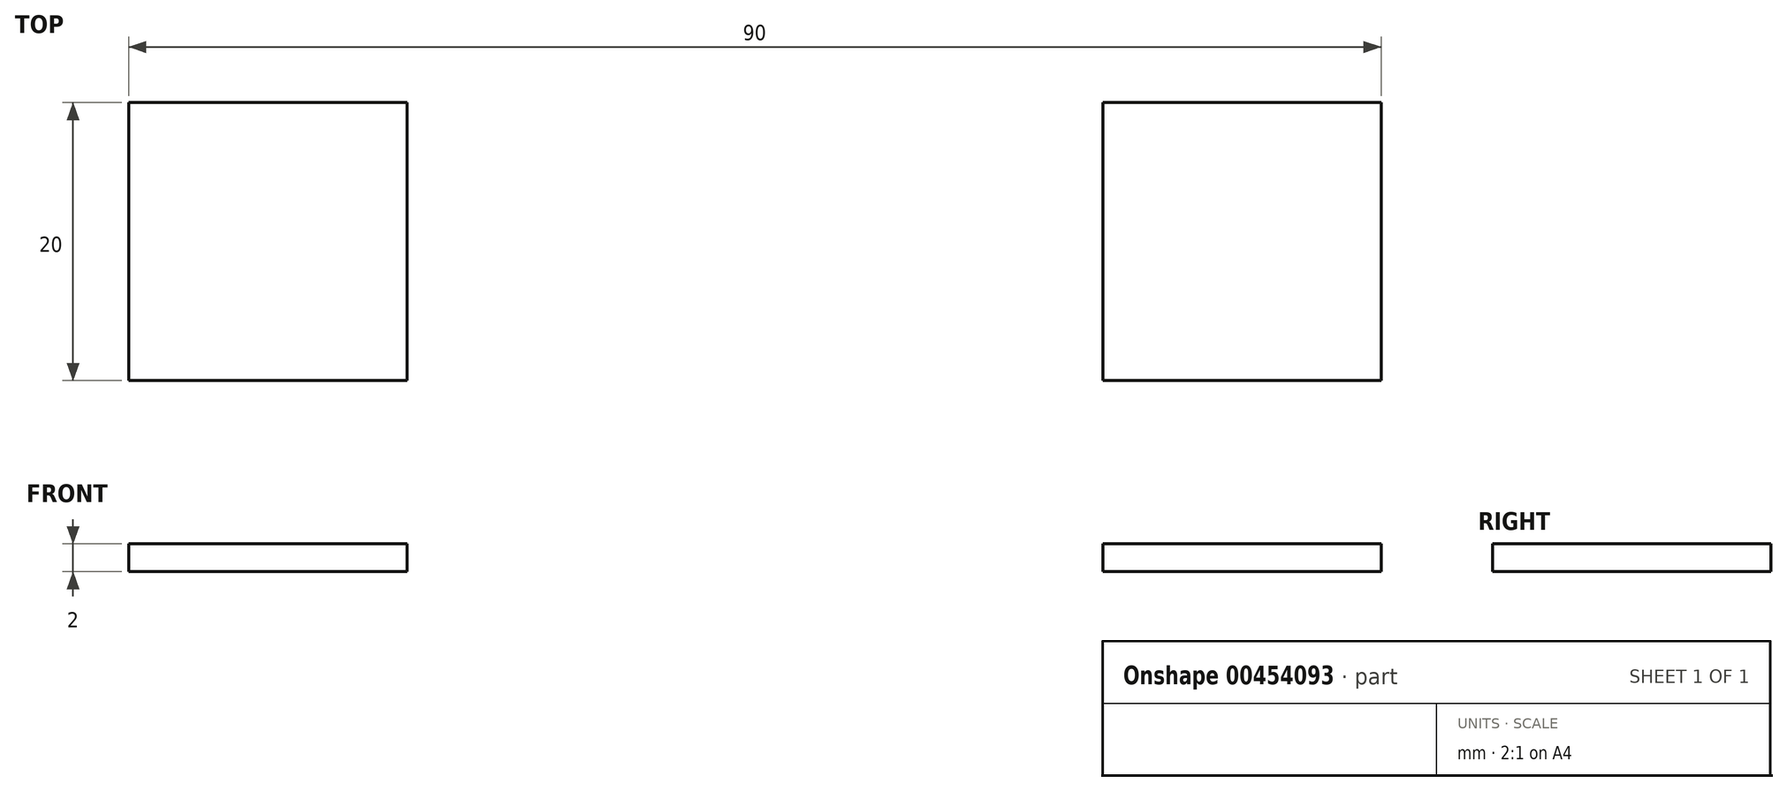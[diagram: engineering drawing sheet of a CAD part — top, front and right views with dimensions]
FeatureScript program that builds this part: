
annotation { "Feature Type Name" : "Feature", "Feature Type Description" : "" }
export const myFeature = defineFeature(function(context is Context, id is Id, definition is map)
    precondition{}
    {
        {
            var Q0;
            Q0=qCreatedBy(makeId("Top.planeOp"),FACE);
            var sketch = newSketch(context, id + "F0", { "sketchPlane" : qUnion([Q0])});
            skLineSegment(sketch, "E0.bottom", {"start": v(-45, 26.01) * mm, "end": v(45, 26.01) * mm});
            skLineSegment(sketch, "E0.top", {"start": v(-45, -15.49) * mm, "end": v(45, -15.49) * mm});
            skLineSegment(sketch, "E0.left", {"start": v(-45, 26.01) * mm, "end": v(-45, -15.49) * mm});
            skLineSegment(sketch, "E0.right", {"start": v(45, 26.01) * mm, "end": v(45, -15.49) * mm});
            skLineSegment(sketch, "E1.bottom", {"start": v(-18.4, 18.51) * mm, "end": v(-14.9, 18.51) * mm});
            skLineSegment(sketch, "E1.top", {"start": v(-18.4, 2.51) * mm, "end": v(-14.9, 2.51) * mm});
            skLineSegment(sketch, "E1.left", {"start": v(-18.4, 18.51) * mm, "end": v(-18.4, 2.51) * mm});
            skLineSegment(sketch, "E1.right", {"start": v(-14.9, 18.51) * mm, "end": v(-14.9, 2.51) * mm});
            skPoint(sketch, "E2", {"position": v(0, 26.01) * mm});
            skLineSegment(sketch, "E3.MirrorCS", {"start": v(14.9, 18.51) * mm, "end": v(14.9, 2.51) * mm});
            skLineSegment(sketch, "E4.MirrorCS", {"start": v(18.4, 18.51) * mm, "end": v(14.9, 18.51) * mm});
            skLineSegment(sketch, "E5.MirrorCS", {"start": v(18.4, 18.51) * mm, "end": v(18.4, 2.51) * mm});
            skLineSegment(sketch, "E6.MirrorCS", {"start": v(18.4, 2.51) * mm, "end": v(14.9, 2.51) * mm});
            skLineSegment(sketch, "E7.bottom", {"start": v(-42.16, 0.51) * mm, "end": v(-21.16, 0.51) * mm, "construction": true});
            skLineSegment(sketch, "E7.top", {"start": v(-42.16, -12.99) * mm, "end": v(-21.16, -12.99) * mm, "construction": true});
            skLineSegment(sketch, "E7.left", {"start": v(-42.16, 0.51) * mm, "end": v(-42.16, -12.99) * mm, "construction": true});
            skLineSegment(sketch, "E7.right", {"start": v(-21.16, 0.51) * mm, "end": v(-21.16, -12.99) * mm, "construction": true});
            skLineSegment(sketch, "E8.MirrorCS", {"start": v(21.16, 0.51) * mm, "end": v(21.16, -12.99) * mm, "construction": true});
            skLineSegment(sketch, "E9.MirrorCS", {"start": v(42.16, -12.99) * mm, "end": v(21.16, -12.99) * mm, "construction": true});
            skLineSegment(sketch, "E10.MirrorCS", {"start": v(42.16, 0.51) * mm, "end": v(21.16, 0.51) * mm, "construction": true});
            skLineSegment(sketch, "E11.MirrorCS", {"start": v(42.16, 0.51) * mm, "end": v(42.16, -12.99) * mm, "construction": true});
            skLineSegment(sketch, "E12.bottom", {"start": v(25, 26.01) * mm, "end": v(45, 26.01) * mm});
            skLineSegment(sketch, "E12.top", {"start": v(25, 6.01) * mm, "end": v(45, 6.01) * mm});
            skLineSegment(sketch, "E12.left", {"start": v(25, 26.01) * mm, "end": v(25, 6.01) * mm});
            skLineSegment(sketch, "E12.right", {"start": v(45, 26.01) * mm, "end": v(45, 6.01) * mm});
            skPoint(sketch, "E13.oppositeSnap0", {"position": v(35, 6.01) * mm});
            skLineSegment(sketch, "E14.bottom", {"start": v(-45, 26.01) * mm, "end": v(-25, 26.01) * mm});
            skLineSegment(sketch, "E14.top", {"start": v(-45, 6.01) * mm, "end": v(-25, 6.01) * mm});
            skLineSegment(sketch, "E14.left", {"start": v(-45, 26.01) * mm, "end": v(-45, 6.01) * mm});
            skLineSegment(sketch, "E14.right", {"start": v(-25, 26.01) * mm, "end": v(-25, 6.01) * mm});
            skLineSegment(sketch, "E15.bottom", {"start": v(-14.9, -15.49) * mm, "end": v(14.9, -15.49) * mm});
            skLineSegment(sketch, "E15.top", {"start": v(-14.9, -6.99) * mm, "end": v(14.9, -6.99) * mm});
            skLineSegment(sketch, "E15.left", {"start": v(-14.9, -15.49) * mm, "end": v(-14.9, -6.99) * mm});
            skLineSegment(sketch, "E15.right", {"start": v(14.9, -15.49) * mm, "end": v(14.9, -6.99) * mm});
            skLineSegment(sketch, "E16.bottom", {"start": v(-14.9, -6.99) * mm, "end": v(4.53, -6.99) * mm});
            skLineSegment(sketch, "E16.top", {"start": v(-14.9, -3.99) * mm, "end": v(4.53, -3.99) * mm});
            skLineSegment(sketch, "E16.left", {"start": v(-14.9, -6.99) * mm, "end": v(-14.9, -3.99) * mm});
            skLineSegment(sketch, "E16.right", {"start": v(4.53, -6.99) * mm, "end": v(4.53, -3.99) * mm});
            skSolve(sketch);
        }
        {
            var Q0;
            Q0=makeQuery(id+"F0.imprint","IMPRINT",FACE,{"disambiguationData":[TD([[makeQuery(id+"F0.imprint","IMPRINT",EDGE,{"derivedFrom":sQuery(id+"F0.wireOp",EDGE,"E0.bottom")}),-1.0]])]});
            extrude(context, id + "F1", {"entities" : qUnion([Q0]), "depth" : 2 * mm});
        }
        {
            var Q0;
            Q0=sQuery(id+"F0.wireOp",VERTEX,"E7.bottom.start");
            var Q1;
            Q1=sQuery(id+"F0.wireOp",VERTEX,"E7.bottom.end");
            var Q2;
            Q2=sQuery(id+"F0.wireOp",VERTEX,"E7.top.end");
            var Q3;
            Q3=sQuery(id+"F0.wireOp",VERTEX,"E7.top.start");
            var Q4;
            Q4=sQuery(id+"F0.wireOp",VERTEX,"E8.MirrorCS.end");
            var Q5;
            Q5=sQuery(id+"F0.wireOp",VERTEX,"E8.MirrorCS.start");
            var Q6;
            Q6=sQuery(id+"F0.wireOp",VERTEX,"E10.MirrorCS.start");
            var Q7;
            Q7=sQuery(id+"F0.wireOp",VERTEX,"E11.MirrorCS.end");
            var Q8;
            Q8=makeQuery(id+"F1.opExtrude","SWEPT_BODY",BODY,{"disambiguationData":[OSD([sQuery(id+"F0.wireOp",EDGE,"E0.bottom"),sQuery(id+"F0.wireOp",EDGE,"E0.top"),sQuery(id+"F0.wireOp",EDGE,"E0.left"),sQuery(id+"F0.wireOp",EDGE,"E0.right"),sQuery(id+"F0.wireOp",EDGE,"E1.bottom"),sQuery(id+"F0.wireOp",EDGE,"E1.top"),sQuery(id+"F0.wireOp",EDGE,"E1.left"),sQuery(id+"F0.wireOp",EDGE,"E1.right"),sQuery(id+"F0.wireOp",EDGE,"E3.MirrorCS"),sQuery(id+"F0.wireOp",EDGE,"E4.MirrorCS"),sQuery(id+"F0.wireOp",EDGE,"E5.MirrorCS"),sQuery(id+"F0.wireOp",EDGE,"E6.MirrorCS")])]});
            hole(context, id + "F2", {"style" : HoleStyle.SIMPLE, "endStyle" : HoleEndStyle.BLIND, "oppositeDirection" : true, "standardTappedOrClearance" : lookupTablePath({ "standard" : "ISO", "fit" : "Close", "size" : "M3", "type" : "Clearance" }), "standardBlindInLast" : lookupTablePath({ "fit" : "Close", "standard" : "ISO", "size" : "M3", "type" : "Clearance" }), "holeDiameter" : 3.15 * mm, "holeDepth" : 15 * mm, "isTappedThrough" : true, "tappedDepth" : 12 * mm, "tapClearance" : 3, "locations" : qUnion([Q0, Q1, Q2, Q3, Q4, Q5, Q6, Q7]), "scope" : qUnion([Q8])});
        }
    });
